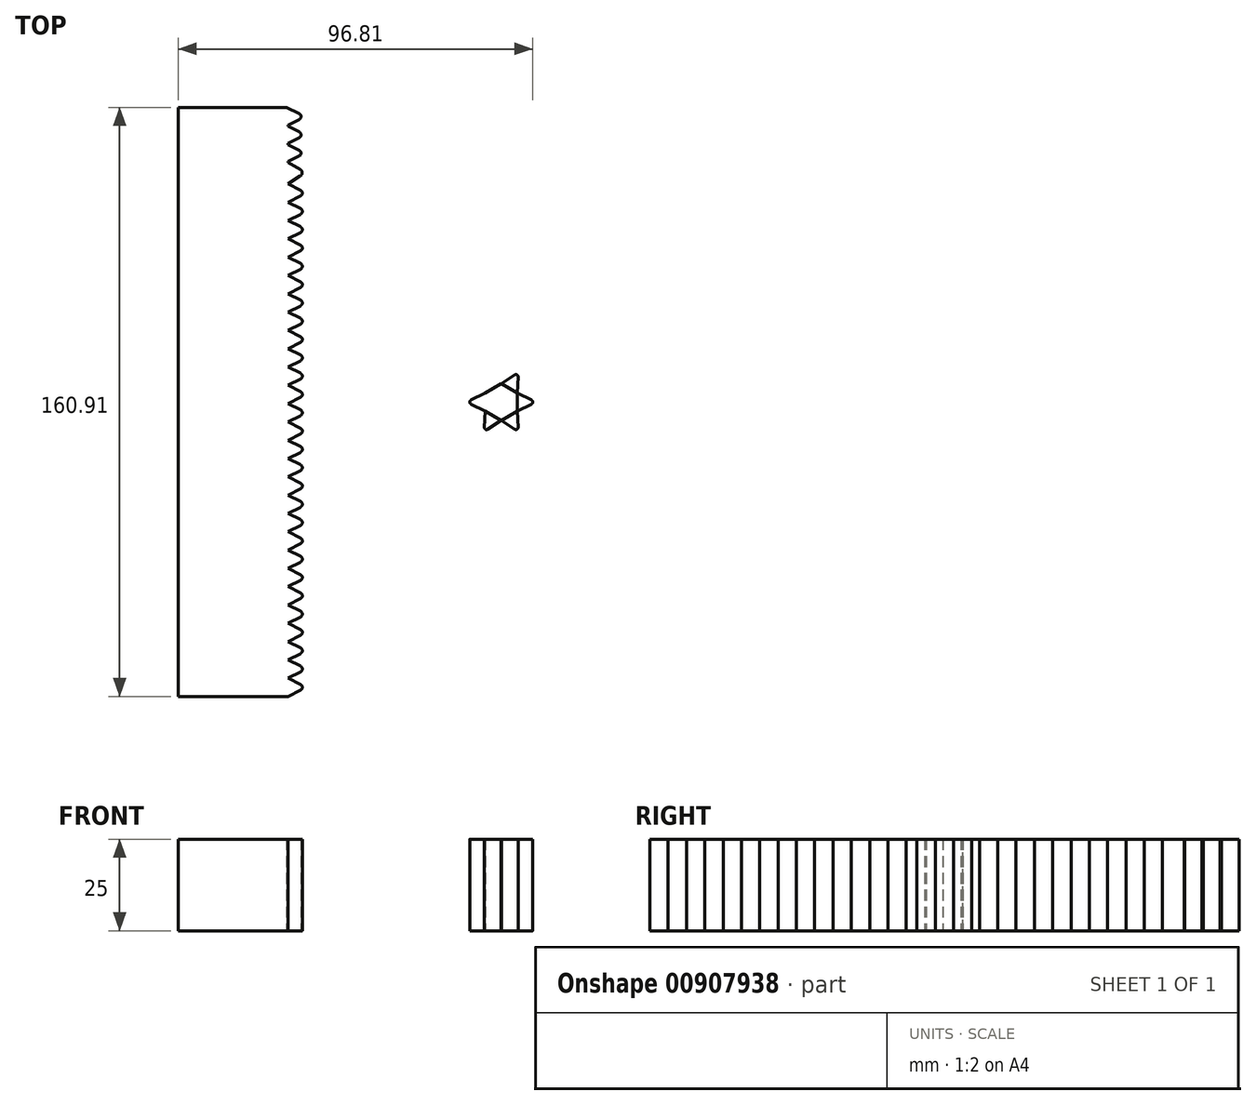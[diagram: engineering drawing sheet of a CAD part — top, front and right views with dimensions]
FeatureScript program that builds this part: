
annotation { "Feature Type Name" : "Feature", "Feature Type Description" : "" }
export const myFeature = defineFeature(function(context is Context, id is Id, definition is map)
    precondition{}
    {
        {
            var Q0;
            Q0=qCreatedBy(makeId("Top.planeOp"),FACE);
            var sketch = newSketch(context, id + "F0", { "sketchPlane" : qUnion([Q0])});
            skLineSegment(sketch, "E0.top", {"start": v(-93.92, -77.91) * mm, "end": v(-63.92, -77.91) * mm});
            skLineSegment(sketch, "E1.right", {"start": v(-63.92, -72.91) * mm, "end": v(-63.92, -77.91) * mm});
            skLineSegment(sketch, "E2", {"start": v(-63.92, -72.91) * mm, "end": v(-60.51, -74.61) * mm});
            skLineSegment(sketch, "E3", {"start": v(-60.51, -76.21) * mm, "end": v(-63.92, -77.91) * mm});
            skLineSegment(sketch, "E4.right", {"start": v(-63.92, -67.91) * mm, "end": v(-63.92, -72.91) * mm});
            skLineSegment(sketch, "E5", {"start": v(-63.92, -67.91) * mm, "end": v(-60.51, -69.61) * mm});
            skLineSegment(sketch, "E6", {"start": v(-60.51, -71.21) * mm, "end": v(-63.92, -72.91) * mm});
            skLineSegment(sketch, "E7.right", {"start": v(-63.92, -62.91) * mm, "end": v(-63.92, -67.91) * mm});
            skLineSegment(sketch, "E8", {"start": v(-63.92, -62.91) * mm, "end": v(-60.51, -64.61) * mm});
            skLineSegment(sketch, "E9", {"start": v(-60.51, -66.21) * mm, "end": v(-63.92, -67.91) * mm});
            skLineSegment(sketch, "E10.right", {"start": v(-63.92, -57.91) * mm, "end": v(-63.92, -62.91) * mm});
            skLineSegment(sketch, "E11", {"start": v(-63.92, -57.91) * mm, "end": v(-60.51, -59.61) * mm});
            skLineSegment(sketch, "E12", {"start": v(-60.51, -61.21) * mm, "end": v(-63.92, -62.91) * mm});
            skLineSegment(sketch, "E13.right", {"start": v(-63.92, -52.91) * mm, "end": v(-63.92, -57.91) * mm});
            skLineSegment(sketch, "E14", {"start": v(-63.92, -52.91) * mm, "end": v(-60.51, -54.61) * mm});
            skLineSegment(sketch, "E15", {"start": v(-60.51, -56.21) * mm, "end": v(-63.92, -57.91) * mm});
            skLineSegment(sketch, "E16.right", {"start": v(-63.92, -47.91) * mm, "end": v(-63.92, -52.91) * mm});
            skLineSegment(sketch, "E17", {"start": v(-63.92, -47.91) * mm, "end": v(-60.51, -49.61) * mm});
            skLineSegment(sketch, "E18", {"start": v(-60.51, -51.21) * mm, "end": v(-63.92, -52.91) * mm});
            skLineSegment(sketch, "E19.right", {"start": v(-63.92, -42.91) * mm, "end": v(-63.92, -47.91) * mm});
            skLineSegment(sketch, "E20", {"start": v(-63.92, -42.91) * mm, "end": v(-60.51, -44.61) * mm});
            skLineSegment(sketch, "E21", {"start": v(-60.51, -46.21) * mm, "end": v(-63.92, -47.91) * mm});
            skLineSegment(sketch, "E22.right", {"start": v(-63.92, -37.91) * mm, "end": v(-63.92, -42.91) * mm});
            skLineSegment(sketch, "E23", {"start": v(-63.92, -37.91) * mm, "end": v(-60.51, -39.61) * mm});
            skLineSegment(sketch, "E24", {"start": v(-60.51, -41.21) * mm, "end": v(-63.92, -42.91) * mm});
            skLineSegment(sketch, "E25.right", {"start": v(-63.92, -32.91) * mm, "end": v(-63.92, -37.91) * mm});
            skLineSegment(sketch, "E26", {"start": v(-63.92, -32.91) * mm, "end": v(-60.51, -34.61) * mm});
            skLineSegment(sketch, "E27", {"start": v(-60.51, -36.21) * mm, "end": v(-63.92, -37.91) * mm});
            skLineSegment(sketch, "E28.right", {"start": v(-63.92, -27.91) * mm, "end": v(-63.92, -32.91) * mm});
            skLineSegment(sketch, "E29", {"start": v(-63.92, -27.91) * mm, "end": v(-60.51, -29.61) * mm});
            skLineSegment(sketch, "E30", {"start": v(-60.51, -31.21) * mm, "end": v(-63.92, -32.91) * mm});
            skLineSegment(sketch, "E31.right", {"start": v(-63.92, -22.91) * mm, "end": v(-63.92, -27.91) * mm});
            skLineSegment(sketch, "E32", {"start": v(-63.92, -22.91) * mm, "end": v(-60.51, -24.61) * mm});
            skLineSegment(sketch, "E33", {"start": v(-60.51, -26.21) * mm, "end": v(-63.92, -27.91) * mm});
            skLineSegment(sketch, "E34.right", {"start": v(-63.92, -17.91) * mm, "end": v(-63.92, -22.91) * mm});
            skLineSegment(sketch, "E35", {"start": v(-63.92, -17.91) * mm, "end": v(-60.51, -19.61) * mm});
            skLineSegment(sketch, "E36", {"start": v(-60.51, -21.21) * mm, "end": v(-63.92, -22.91) * mm});
            skLineSegment(sketch, "E37.right", {"start": v(-63.92, -12.91) * mm, "end": v(-63.92, -17.91) * mm});
            skLineSegment(sketch, "E38", {"start": v(-63.92, -12.91) * mm, "end": v(-60.51, -14.61) * mm});
            skLineSegment(sketch, "E39", {"start": v(-60.51, -16.21) * mm, "end": v(-63.92, -17.91) * mm});
            skLineSegment(sketch, "E40.right", {"start": v(-63.92, -7.91) * mm, "end": v(-63.92, -12.91) * mm});
            skLineSegment(sketch, "E41", {"start": v(-63.92, -7.91) * mm, "end": v(-60.51, -9.61) * mm});
            skLineSegment(sketch, "E42", {"start": v(-60.51, -11.21) * mm, "end": v(-63.92, -12.91) * mm});
            skLineSegment(sketch, "E43.right", {"start": v(-63.92, -2.91) * mm, "end": v(-63.92, -7.91) * mm});
            skLineSegment(sketch, "E44", {"start": v(-63.92, -2.91) * mm, "end": v(-60.51, -4.61) * mm});
            skLineSegment(sketch, "E45", {"start": v(-60.51, -6.21) * mm, "end": v(-63.92, -7.91) * mm});
            skLineSegment(sketch, "E46.right", {"start": v(-63.92, 2.09) * mm, "end": v(-63.92, -2.91) * mm});
            skLineSegment(sketch, "E47", {"start": v(-63.92, 2.09) * mm, "end": v(-60.51, 0.39) * mm});
            skLineSegment(sketch, "E48", {"start": v(-60.51, -1.21) * mm, "end": v(-63.92, -2.91) * mm});
            skLineSegment(sketch, "E49.right", {"start": v(-63.92, 7.09) * mm, "end": v(-63.92, 2.09) * mm});
            skLineSegment(sketch, "E50", {"start": v(-63.92, 7.09) * mm, "end": v(-60.51, 5.39) * mm});
            skLineSegment(sketch, "E51", {"start": v(-60.51, 3.79) * mm, "end": v(-63.92, 2.09) * mm});
            skLineSegment(sketch, "E52.right", {"start": v(-63.92, 12.09) * mm, "end": v(-63.92, 7.09) * mm});
            skLineSegment(sketch, "E53", {"start": v(-63.92, 12.09) * mm, "end": v(-60.51, 10.39) * mm});
            skLineSegment(sketch, "E54", {"start": v(-60.51, 8.79) * mm, "end": v(-63.92, 7.09) * mm});
            skLineSegment(sketch, "E55.right", {"start": v(-63.92, 17.09) * mm, "end": v(-63.92, 12.09) * mm});
            skLineSegment(sketch, "E56", {"start": v(-63.92, 17.09) * mm, "end": v(-60.51, 15.39) * mm});
            skLineSegment(sketch, "E57", {"start": v(-60.51, 13.79) * mm, "end": v(-63.92, 12.09) * mm});
            skLineSegment(sketch, "E58.right", {"start": v(-63.92, 22.09) * mm, "end": v(-63.92, 17.09) * mm});
            skLineSegment(sketch, "E59", {"start": v(-63.92, 22.09) * mm, "end": v(-60.51, 20.39) * mm});
            skLineSegment(sketch, "E60", {"start": v(-60.51, 18.79) * mm, "end": v(-63.92, 17.09) * mm});
            skLineSegment(sketch, "E61.right", {"start": v(-63.92, 27.09) * mm, "end": v(-63.92, 22.09) * mm});
            skLineSegment(sketch, "E62", {"start": v(-63.92, 27.09) * mm, "end": v(-60.51, 25.39) * mm});
            skLineSegment(sketch, "E63", {"start": v(-60.51, 23.79) * mm, "end": v(-63.92, 22.09) * mm});
            skLineSegment(sketch, "E64.right", {"start": v(-63.92, 32.09) * mm, "end": v(-63.92, 27.09) * mm});
            skLineSegment(sketch, "E65", {"start": v(-63.92, 32.09) * mm, "end": v(-60.51, 30.39) * mm});
            skLineSegment(sketch, "E66", {"start": v(-60.51, 28.79) * mm, "end": v(-63.92, 27.09) * mm});
            skLineSegment(sketch, "E67.right", {"start": v(-63.92, 37.09) * mm, "end": v(-63.92, 32.09) * mm});
            skLineSegment(sketch, "E68", {"start": v(-63.92, 37.09) * mm, "end": v(-60.51, 35.39) * mm});
            skLineSegment(sketch, "E69", {"start": v(-60.51, 33.79) * mm, "end": v(-63.92, 32.09) * mm});
            skLineSegment(sketch, "E70.right", {"start": v(-63.92, 42.09) * mm, "end": v(-63.92, 37.09) * mm});
            skLineSegment(sketch, "E71", {"start": v(-63.92, 42.09) * mm, "end": v(-60.51, 40.39) * mm});
            skLineSegment(sketch, "E72", {"start": v(-60.51, 38.79) * mm, "end": v(-63.92, 37.09) * mm});
            skLineSegment(sketch, "E73.right", {"start": v(-63.92, 47.09) * mm, "end": v(-63.92, 42.09) * mm});
            skLineSegment(sketch, "E74", {"start": v(-63.92, 47.09) * mm, "end": v(-60.51, 45.39) * mm});
            skLineSegment(sketch, "E75", {"start": v(-60.51, 43.79) * mm, "end": v(-63.92, 42.09) * mm});
            skLineSegment(sketch, "E76.right", {"start": v(-63.92, 52.09) * mm, "end": v(-63.92, 47.09) * mm});
            skLineSegment(sketch, "E77", {"start": v(-63.92, 52.09) * mm, "end": v(-60.51, 50.39) * mm});
            skLineSegment(sketch, "E78", {"start": v(-60.51, 48.79) * mm, "end": v(-63.92, 47.09) * mm});
            skLineSegment(sketch, "E79.right", {"start": v(-63.92, 57.09) * mm, "end": v(-63.92, 52.09) * mm});
            skLineSegment(sketch, "E80", {"start": v(-63.92, 57.09) * mm, "end": v(-60.51, 55.39) * mm});
            skLineSegment(sketch, "E81", {"start": v(-60.51, 53.79) * mm, "end": v(-63.92, 52.09) * mm});
            skLineSegment(sketch, "E82.right", {"start": v(-63.92, 62.09) * mm, "end": v(-63.92, 57.09) * mm});
            skLineSegment(sketch, "E83", {"start": v(-63.92, 62.09) * mm, "end": v(-60.51, 60.39) * mm});
            skLineSegment(sketch, "E84", {"start": v(-60.51, 58.79) * mm, "end": v(-63.92, 57.09) * mm});
            skLineSegment(sketch, "E85.right", {"start": v(-63.92, 68) * mm, "end": v(-63.92, 62.09) * mm});
            skLineSegment(sketch, "E86", {"start": v(-63.92, 68) * mm, "end": v(-60.62, 66.1) * mm});
            skLineSegment(sketch, "E87", {"start": v(-60.58, 64.23) * mm, "end": v(-63.92, 62.08) * mm});
            skLineSegment(sketch, "E88.right", {"start": v(-63.92, 73) * mm, "end": v(-63.92, 68) * mm});
            skLineSegment(sketch, "E89", {"start": v(-64.28, 73) * mm, "end": v(-60.88, 71.3) * mm});
            skLineSegment(sketch, "E90", {"start": v(-60.88, 69.7) * mm, "end": v(-63.92, 68.18) * mm});
            skLineSegment(sketch, "E91.right", {"start": v(-63.92, 78) * mm, "end": v(-63.92, 73) * mm});
            skLineSegment(sketch, "E92", {"start": v(-64.28, 78) * mm, "end": v(-60.88, 76.3) * mm});
            skLineSegment(sketch, "E93", {"start": v(-60.88, 74.7) * mm, "end": v(-63.92, 73.18) * mm});
            skLineSegment(sketch, "E94.right", {"start": v(-63.92, 83) * mm, "end": v(-63.92, 78) * mm});
            skLineSegment(sketch, "E95", {"start": v(-64.28, 83) * mm, "end": v(-60.88, 81.3) * mm});
            skLineSegment(sketch, "E96", {"start": v(-60.88, 79.7) * mm, "end": v(-63.92, 78.18) * mm});
            skPoint(sketch, "E97.visualSharp", {"position": v(-59.28, 80.5) * mm});
            skArc(sketch, "E97.filletArc", {"start": v(-60.88, 79.7) * mm, "mid": v(-60.38, 80.5) * mm, "end": v(-60.88, 81.3) * mm});
            skPoint(sketch, "E98.visualSharp", {"position": v(-59.28, 75.5) * mm});
            skArc(sketch, "E98.filletArc", {"start": v(-60.88, 74.7) * mm, "mid": v(-60.38, 75.5) * mm, "end": v(-60.88, 76.3) * mm});
            skPoint(sketch, "E99.visualSharp", {"position": v(-59.28, 70.5) * mm});
            skArc(sketch, "E99.filletArc", {"start": v(-60.88, 69.7) * mm, "mid": v(-60.38, 70.5) * mm, "end": v(-60.88, 71.3) * mm});
            skPoint(sketch, "E100.visualSharp", {"position": v(-59.08, 65.2) * mm});
            skArc(sketch, "E100.filletArc", {"start": v(-60.58, 64.23) * mm, "mid": v(-60.08, 65.18) * mm, "end": v(-60.62, 66.1) * mm});
            skPoint(sketch, "E101.visualSharp", {"position": v(-58.92, 59.59) * mm});
            skArc(sketch, "E101.filletArc", {"start": v(-60.51, 58.79) * mm, "mid": v(-60.02, 59.59) * mm, "end": v(-60.51, 60.39) * mm});
            skPoint(sketch, "E102.visualSharp", {"position": v(-58.92, 54.59) * mm});
            skArc(sketch, "E102.filletArc", {"start": v(-60.51, 53.79) * mm, "mid": v(-60.02, 54.59) * mm, "end": v(-60.51, 55.39) * mm});
            skPoint(sketch, "E103.visualSharp", {"position": v(-58.92, 49.59) * mm});
            skArc(sketch, "E103.filletArc", {"start": v(-60.51, 48.79) * mm, "mid": v(-60.02, 49.59) * mm, "end": v(-60.51, 50.39) * mm});
            skPoint(sketch, "E104.visualSharp", {"position": v(-58.92, 44.59) * mm});
            skArc(sketch, "E104.filletArc", {"start": v(-60.51, 43.79) * mm, "mid": v(-60.02, 44.59) * mm, "end": v(-60.51, 45.39) * mm});
            skPoint(sketch, "E105.visualSharp", {"position": v(-58.92, 39.59) * mm});
            skArc(sketch, "E105.filletArc", {"start": v(-60.51, 38.79) * mm, "mid": v(-60.02, 39.59) * mm, "end": v(-60.51, 40.39) * mm});
            skPoint(sketch, "E106.visualSharp", {"position": v(-58.92, 34.59) * mm});
            skArc(sketch, "E106.filletArc", {"start": v(-60.51, 33.79) * mm, "mid": v(-60.02, 34.59) * mm, "end": v(-60.51, 35.39) * mm});
            skPoint(sketch, "E107.visualSharp", {"position": v(-58.92, 29.59) * mm});
            skArc(sketch, "E107.filletArc", {"start": v(-60.51, 28.79) * mm, "mid": v(-60.02, 29.59) * mm, "end": v(-60.51, 30.39) * mm});
            skPoint(sketch, "E108.visualSharp", {"position": v(-58.92, 24.59) * mm});
            skArc(sketch, "E108.filletArc", {"start": v(-60.51, 23.79) * mm, "mid": v(-60.02, 24.59) * mm, "end": v(-60.51, 25.39) * mm});
            skPoint(sketch, "E109.visualSharp", {"position": v(-58.92, 19.59) * mm});
            skArc(sketch, "E109.filletArc", {"start": v(-60.51, 18.79) * mm, "mid": v(-60.02, 19.59) * mm, "end": v(-60.51, 20.39) * mm});
            skPoint(sketch, "E110.visualSharp", {"position": v(-58.92, 14.59) * mm});
            skArc(sketch, "E110.filletArc", {"start": v(-60.51, 13.79) * mm, "mid": v(-60.02, 14.59) * mm, "end": v(-60.51, 15.39) * mm});
            skPoint(sketch, "E111.visualSharp", {"position": v(-58.92, 9.59) * mm});
            skArc(sketch, "E111.filletArc", {"start": v(-60.51, 8.79) * mm, "mid": v(-60.02, 9.59) * mm, "end": v(-60.51, 10.39) * mm});
            skPoint(sketch, "E112.visualSharp", {"position": v(-58.92, 4.59) * mm});
            skArc(sketch, "E112.filletArc", {"start": v(-60.51, 3.79) * mm, "mid": v(-60.02, 4.59) * mm, "end": v(-60.51, 5.39) * mm});
            skPoint(sketch, "E113.visualSharp", {"position": v(-58.92, -0.41) * mm});
            skArc(sketch, "E113.filletArc", {"start": v(-60.51, -1.21) * mm, "mid": v(-60.02, -0.41) * mm, "end": v(-60.51, 0.39) * mm});
            skPoint(sketch, "E114.visualSharp", {"position": v(-58.92, -5.41) * mm});
            skArc(sketch, "E114.filletArc", {"start": v(-60.51, -6.21) * mm, "mid": v(-60.02, -5.41) * mm, "end": v(-60.51, -4.61) * mm});
            skPoint(sketch, "E115.visualSharp", {"position": v(-58.92, -10.41) * mm});
            skArc(sketch, "E115.filletArc", {"start": v(-60.51, -11.21) * mm, "mid": v(-60.02, -10.41) * mm, "end": v(-60.51, -9.61) * mm});
            skPoint(sketch, "E116.visualSharp", {"position": v(-58.92, -15.41) * mm});
            skArc(sketch, "E116.filletArc", {"start": v(-60.51, -16.21) * mm, "mid": v(-60.02, -15.41) * mm, "end": v(-60.51, -14.61) * mm});
            skPoint(sketch, "E117.visualSharp", {"position": v(-58.92, -20.41) * mm});
            skArc(sketch, "E117.filletArc", {"start": v(-60.51, -21.21) * mm, "mid": v(-60.02, -20.41) * mm, "end": v(-60.51, -19.61) * mm});
            skPoint(sketch, "E118.visualSharp", {"position": v(-58.92, -25.41) * mm});
            skArc(sketch, "E118.filletArc", {"start": v(-60.51, -26.21) * mm, "mid": v(-60.02, -25.41) * mm, "end": v(-60.51, -24.61) * mm});
            skPoint(sketch, "E119.visualSharp", {"position": v(-58.92, -30.41) * mm});
            skArc(sketch, "E119.filletArc", {"start": v(-60.51, -31.21) * mm, "mid": v(-60.02, -30.41) * mm, "end": v(-60.51, -29.61) * mm});
            skPoint(sketch, "E120.visualSharp", {"position": v(-58.92, -35.41) * mm});
            skArc(sketch, "E120.filletArc", {"start": v(-60.51, -36.21) * mm, "mid": v(-60.02, -35.41) * mm, "end": v(-60.51, -34.61) * mm});
            skPoint(sketch, "E121.visualSharp", {"position": v(-58.92, -40.41) * mm});
            skArc(sketch, "E121.filletArc", {"start": v(-60.51, -41.21) * mm, "mid": v(-60.02, -40.41) * mm, "end": v(-60.51, -39.61) * mm});
            skPoint(sketch, "E122.visualSharp", {"position": v(-58.92, -45.41) * mm});
            skArc(sketch, "E122.filletArc", {"start": v(-60.51, -46.21) * mm, "mid": v(-60.02, -45.41) * mm, "end": v(-60.51, -44.61) * mm});
            skPoint(sketch, "E123.visualSharp", {"position": v(-58.92, -50.41) * mm});
            skArc(sketch, "E123.filletArc", {"start": v(-60.51, -51.21) * mm, "mid": v(-60.02, -50.41) * mm, "end": v(-60.51, -49.61) * mm});
            skPoint(sketch, "E124.visualSharp", {"position": v(-58.92, -55.41) * mm});
            skArc(sketch, "E124.filletArc", {"start": v(-60.51, -56.21) * mm, "mid": v(-60.02, -55.41) * mm, "end": v(-60.51, -54.61) * mm});
            skPoint(sketch, "E125.visualSharp", {"position": v(-58.92, -60.41) * mm});
            skArc(sketch, "E125.filletArc", {"start": v(-60.51, -61.21) * mm, "mid": v(-60.02, -60.41) * mm, "end": v(-60.51, -59.61) * mm});
            skPoint(sketch, "E126.visualSharp", {"position": v(-58.92, -65.41) * mm});
            skArc(sketch, "E126.filletArc", {"start": v(-60.51, -66.21) * mm, "mid": v(-60.02, -65.41) * mm, "end": v(-60.51, -64.61) * mm});
            skPoint(sketch, "E127.visualSharp", {"position": v(-58.92, -70.41) * mm});
            skArc(sketch, "E127.filletArc", {"start": v(-60.51, -71.21) * mm, "mid": v(-60.02, -70.41) * mm, "end": v(-60.51, -69.61) * mm});
            skPoint(sketch, "E128.visualSharp", {"position": v(-58.92, -75.41) * mm});
            skArc(sketch, "E128.filletArc", {"start": v(-60.51, -76.21) * mm, "mid": v(-60.02, -75.41) * mm, "end": v(-60.51, -74.61) * mm});
            skLineSegment(sketch, "E129", {"start": v(-63.92, 83) * mm, "end": v(-93.92, 83) * mm});
            skLineSegment(sketch, "E130", {"start": v(-93.92, 83) * mm, "end": v(-93.92, -77.91) * mm});
            skSolve(sketch);
        }
        {
            var Q0;
            Q0=makeQuery(id+"F0.imprint","IMPRINT",FACE,{"disambiguationData":[TD([[makeQuery(id+"F0.imprint","IMPRINT",EDGE,{"derivedFrom":sQuery(id+"F0.wireOp",EDGE,"E0.top")}),1.0]])]});
            var Q1;
            Q1=makeQuery(id+"F0.imprint","IMPRINT",FACE,{"disambiguationData":[TD([[makeQuery(id+"F0.imprint","IMPRINT",EDGE,{"derivedFrom":sQuery(id+"F0.wireOp",EDGE,"E52.right")}),1.0]])]});
            var Q2;
            Q2=makeQuery(id+"F0.imprint","IMPRINT",FACE,{"disambiguationData":[TD([[makeQuery(id+"F0.imprint","IMPRINT",EDGE,{"derivedFrom":sQuery(id+"F0.wireOp",EDGE,"E22.right")}),1.0]])]});
            var Q3;
            Q3=makeQuery(id+"F0.imprint","IMPRINT",FACE,{"disambiguationData":[TD([[makeQuery(id+"F0.imprint","IMPRINT",EDGE,{"derivedFrom":sQuery(id+"F0.wireOp",EDGE,"E70.right")}),1.0]])]});
            var Q4;
            Q4=makeQuery(id+"F0.imprint","IMPRINT",FACE,{"disambiguationData":[TD([[makeQuery(id+"F0.imprint","IMPRINT",EDGE,{"derivedFrom":sQuery(id+"F0.wireOp",EDGE,"E13.right")}),1.0]])]});
            var Q5;
            Q5=makeQuery(id+"F0.imprint","IMPRINT",FACE,{"disambiguationData":[TD([[makeQuery(id+"F0.imprint","IMPRINT",EDGE,{"derivedFrom":sQuery(id+"F0.wireOp",EDGE,"E91.right")}),1.0]])]});
            var Q6;
            Q6=makeQuery(id+"F0.imprint","IMPRINT",FACE,{"disambiguationData":[TD([[makeQuery(id+"F0.imprint","IMPRINT",EDGE,{"derivedFrom":sQuery(id+"F0.wireOp",EDGE,"E61.right")}),1.0]])]});
            var Q7;
            Q7=makeQuery(id+"F0.imprint","IMPRINT",FACE,{"disambiguationData":[TD([[makeQuery(id+"F0.imprint","IMPRINT",EDGE,{"derivedFrom":sQuery(id+"F0.wireOp",EDGE,"E31.right")}),1.0]])]});
            var Q8;
            Q8=makeQuery(id+"F0.imprint","IMPRINT",FACE,{"disambiguationData":[TD([[makeQuery(id+"F0.imprint","IMPRINT",EDGE,{"derivedFrom":sQuery(id+"F0.wireOp",EDGE,"E4.right")}),1.0]])]});
            var Q9;
            Q9=makeQuery(id+"F0.imprint","IMPRINT",FACE,{"disambiguationData":[TD([[makeQuery(id+"F0.imprint","IMPRINT",EDGE,{"derivedFrom":sQuery(id+"F0.wireOp",EDGE,"E43.right")}),1.0]])]});
            var Q10;
            Q10=makeQuery(id+"F0.imprint","IMPRINT",FACE,{"disambiguationData":[TD([[makeQuery(id+"F0.imprint","IMPRINT",EDGE,{"derivedFrom":sQuery(id+"F0.wireOp",EDGE,"E79.right")}),1.0]])]});
            var Q11;
            Q11=makeQuery(id+"F0.imprint","IMPRINT",FACE,{"disambiguationData":[TD([[makeQuery(id+"F0.imprint","IMPRINT",EDGE,{"derivedFrom":sQuery(id+"F0.wireOp",EDGE,"E85.right")}),1.0]])]});
            var Q12;
            Q12=makeQuery(id+"F0.imprint","IMPRINT",FACE,{"disambiguationData":[TD([[makeQuery(id+"F0.imprint","IMPRINT",EDGE,{"derivedFrom":sQuery(id+"F0.wireOp",EDGE,"E55.right")}),1.0]])]});
            var Q13;
            Q13=makeQuery(id+"F0.imprint","IMPRINT",FACE,{"disambiguationData":[TD([[makeQuery(id+"F0.imprint","IMPRINT",EDGE,{"derivedFrom":sQuery(id+"F0.wireOp",EDGE,"E40.right")}),1.0]])]});
            var Q14;
            Q14=makeQuery(id+"F0.imprint","IMPRINT",FACE,{"disambiguationData":[TD([[makeQuery(id+"F0.imprint","IMPRINT",EDGE,{"derivedFrom":sQuery(id+"F0.wireOp",EDGE,"E7.right")}),1.0]])]});
            var Q15;
            {var subQ1=sQuery(id+"F0.wireOp",EDGE,"E95");Q15=makeQuery(id+"F0.imprint","IMPRINT",FACE,{"disambiguationData":[TD([[makeQuery(id+"F0.imprint","IMPRINT",EDGE,{"derivedFrom":subQ1}),-1.0]])]});}
            var Q16;
            Q16=makeQuery(id+"F0.imprint","IMPRINT",FACE,{"disambiguationData":[TD([[makeQuery(id+"F0.imprint","IMPRINT",EDGE,{"derivedFrom":sQuery(id+"F0.wireOp",EDGE,"E67.right")}),1.0]])]});
            var Q17;
            Q17=makeQuery(id+"F0.imprint","IMPRINT",FACE,{"disambiguationData":[TD([[makeQuery(id+"F0.imprint","IMPRINT",EDGE,{"derivedFrom":sQuery(id+"F0.wireOp",EDGE,"E73.right")}),1.0]])]});
            var Q18;
            Q18=makeQuery(id+"F0.imprint","IMPRINT",FACE,{"disambiguationData":[TD([[makeQuery(id+"F0.imprint","IMPRINT",EDGE,{"derivedFrom":sQuery(id+"F0.wireOp",EDGE,"E19.right")}),1.0]])]});
            var Q19;
            Q19=makeQuery(id+"F0.imprint","IMPRINT",FACE,{"disambiguationData":[TD([[makeQuery(id+"F0.imprint","IMPRINT",EDGE,{"derivedFrom":sQuery(id+"F0.wireOp",EDGE,"E88.right")}),1.0]])]});
            var Q20;
            Q20=makeQuery(id+"F0.imprint","IMPRINT",FACE,{"disambiguationData":[TD([[makeQuery(id+"F0.imprint","IMPRINT",EDGE,{"derivedFrom":sQuery(id+"F0.wireOp",EDGE,"E25.right")}),1.0]])]});
            var Q21;
            Q21=makeQuery(id+"F0.imprint","IMPRINT",FACE,{"disambiguationData":[TD([[makeQuery(id+"F0.imprint","IMPRINT",EDGE,{"derivedFrom":sQuery(id+"F0.wireOp",EDGE,"E82.right")}),1.0]])]});
            var Q22;
            Q22=makeQuery(id+"F0.imprint","IMPRINT",FACE,{"disambiguationData":[TD([[makeQuery(id+"F0.imprint","IMPRINT",EDGE,{"derivedFrom":sQuery(id+"F0.wireOp",EDGE,"E1.right")}),1.0]])]});
            var Q23;
            Q23=makeQuery(id+"F0.imprint","IMPRINT",FACE,{"disambiguationData":[TD([[makeQuery(id+"F0.imprint","IMPRINT",EDGE,{"derivedFrom":sQuery(id+"F0.wireOp",EDGE,"E28.right")}),1.0]])]});
            var Q24;
            Q24=makeQuery(id+"F0.imprint","IMPRINT",FACE,{"disambiguationData":[TD([[makeQuery(id+"F0.imprint","IMPRINT",EDGE,{"derivedFrom":sQuery(id+"F0.wireOp",EDGE,"E76.right")}),1.0]])]});
            var Q25;
            Q25=makeQuery(id+"F0.imprint","IMPRINT",FACE,{"disambiguationData":[TD([[makeQuery(id+"F0.imprint","IMPRINT",EDGE,{"derivedFrom":sQuery(id+"F0.wireOp",EDGE,"E49.right")}),1.0]])]});
            var Q26;
            Q26=makeQuery(id+"F0.imprint","IMPRINT",FACE,{"disambiguationData":[TD([[makeQuery(id+"F0.imprint","IMPRINT",EDGE,{"derivedFrom":sQuery(id+"F0.wireOp",EDGE,"E58.right")}),1.0]])]});
            var Q27;
            Q27=makeQuery(id+"F0.imprint","IMPRINT",FACE,{"disambiguationData":[TD([[makeQuery(id+"F0.imprint","IMPRINT",EDGE,{"derivedFrom":sQuery(id+"F0.wireOp",EDGE,"E37.right")}),1.0]])]});
            var Q28;
            Q28=makeQuery(id+"F0.imprint","IMPRINT",FACE,{"disambiguationData":[TD([[makeQuery(id+"F0.imprint","IMPRINT",EDGE,{"derivedFrom":sQuery(id+"F0.wireOp",EDGE,"E64.right")}),1.0]])]});
            var Q29;
            Q29=makeQuery(id+"F0.imprint","IMPRINT",FACE,{"disambiguationData":[TD([[makeQuery(id+"F0.imprint","IMPRINT",EDGE,{"derivedFrom":sQuery(id+"F0.wireOp",EDGE,"E46.right")}),1.0]])]});
            var Q30;
            Q30=makeQuery(id+"F0.imprint","IMPRINT",FACE,{"disambiguationData":[TD([[makeQuery(id+"F0.imprint","IMPRINT",EDGE,{"derivedFrom":sQuery(id+"F0.wireOp",EDGE,"E10.right")}),1.0]])]});
            var Q31;
            Q31=makeQuery(id+"F0.imprint","IMPRINT",FACE,{"disambiguationData":[TD([[makeQuery(id+"F0.imprint","IMPRINT",EDGE,{"derivedFrom":sQuery(id+"F0.wireOp",EDGE,"E16.right")}),1.0]])]});
            var Q32;
            Q32=makeQuery(id+"F0.imprint","IMPRINT",FACE,{"disambiguationData":[TD([[makeQuery(id+"F0.imprint","IMPRINT",EDGE,{"derivedFrom":sQuery(id+"F0.wireOp",EDGE,"E34.right")}),1.0]])]});
            var Q33;
            {var subQ0=sQuery(id+"F0.wireOp",EDGE,"E84");Q33=makeQuery(id+"F0.imprint","IMPRINT",FACE,{"disambiguationData":[TD([[makeQuery(id+"F0.imprint","IMPRINT",EDGE,{"derivedFrom":subQ0}),-1.0]])]});}
            extrude(context, id + "F1", {"entities" : qUnion([Q0, Q1, Q2, Q3, Q4, Q5, Q6, Q7, Q8, Q9, Q10, Q11, Q12, Q13, Q14, Q15, Q16, Q17, Q18, Q19, Q20, Q21, Q22, Q23, Q24, Q25, Q26, Q27, Q28, Q29, Q30, Q31, Q32, Q33]), "depth" : 25 * mm, "offsetDistance" : 25 * mm});
        }
        {
            var Q0;
            Q0=qCreatedBy(makeId("Top.planeOp"),FACE);
            var sketch = newSketch(context, id + "F2", { "sketchPlane" : qUnion([Q0])});
            skLineSegment(sketch, "E131", {"start": v(-10.04, 5) * mm, "end": v(-10.04, 0) * mm});
            skLineSegment(sketch, "E132", {"start": v(-10.04, 5) * mm, "end": v(-13.97, 3.03) * mm});
            skLineSegment(sketch, "E133", {"start": v(-13.97, 1.97) * mm, "end": v(-10.04, 0) * mm});
            skPoint(sketch, "E134", {"position": v(-10.04, 2.5) * mm});
            skPoint(sketch, "E135.visualSharp", {"position": v(-15.04, 2.5) * mm});
            skArc(sketch, "E135.filletArc", {"start": v(-13.97, 3.03) * mm, "mid": v(-14.3, 2.5) * mm, "end": v(-13.97, 1.97) * mm});
            skLineSegment(sketch, "E136.0", {"start": v(-10.04, 0) * mm, "end": v(-10.04, 5) * mm});
            skLineSegment(sketch, "E136.1", {"start": v(-10.04, 5) * mm, "end": v(-5.7, 7.5) * mm});
            skLineSegment(sketch, "E136.2", {"start": v(-5.7, 7.5) * mm, "end": v(-1.38, 5) * mm});
            skLineSegment(sketch, "E136.3", {"start": v(-1.38, 5) * mm, "end": v(-1.38, 0) * mm});
            skLineSegment(sketch, "E136.4", {"start": v(-1.38, 0) * mm, "end": v(-5.7, -2.5) * mm});
            skLineSegment(sketch, "E136.5", {"start": v(-5.7, -2.5) * mm, "end": v(-10.04, 0) * mm});
            skLineSegment(sketch, "E137", {"start": v(-1.38, 0) * mm, "end": v(2.56, 1.97) * mm});
            skLineSegment(sketch, "E138", {"start": v(2.56, 3.03) * mm, "end": v(-1.38, 5) * mm});
            skArc(sketch, "E139.filletArc", {"start": v(2.56, 1.97) * mm, "mid": v(2.89, 2.5) * mm, "end": v(2.56, 3.03) * mm});
            skLineSegment(sketch, "E140", {"start": v(-10.04, 0) * mm, "end": v(-5.7, -2.5) * mm});
            skLineSegment(sketch, "E141", {"start": v(-10.04, 0) * mm, "end": v(-10.3, -4.4) * mm});
            skLineSegment(sketch, "E142", {"start": v(-9.38, -4.92) * mm, "end": v(-5.7, -2.5) * mm});
            skPoint(sketch, "E143", {"position": v(-7.87, -1.25) * mm});
            skPoint(sketch, "E144.visualSharp", {"position": v(-10.37, -5.58) * mm});
            skArc(sketch, "E144.filletArc", {"start": v(-10.3, -4.4) * mm, "mid": v(-10, -4.94) * mm, "end": v(-9.38, -4.92) * mm});
            skLineSegment(sketch, "E145.3", {"start": v(-5.7, 7.5) * mm, "end": v(-1.37, 5) * mm});
            skLineSegment(sketch, "E145.4", {"start": v(-1.37, 5) * mm, "end": v(-1.37, 0) * mm});
            skLineSegment(sketch, "E145.5", {"start": v(-1.37, 0) * mm, "end": v(-5.7, -2.5) * mm});
            skLineSegment(sketch, "E146", {"start": v(-1.38, 5) * mm, "end": v(-1.11, 9.4) * mm});
            skLineSegment(sketch, "E147", {"start": v(-2.03, 9.92) * mm, "end": v(-5.7, 7.5) * mm});
            skArc(sketch, "E148.filletArc", {"start": v(-1.11, 9.4) * mm, "mid": v(-1.4, 9.94) * mm, "end": v(-2.03, 9.92) * mm});
            skLineSegment(sketch, "E149.0", {"start": v(-10.37, -5.58) * mm, "end": v(-7.87, -1.25) * mm, "construction": true});
            skLineSegment(sketch, "E150", {"start": v(-5.7, -2.5) * mm, "end": v(-1.37, 0) * mm});
            skLineSegment(sketch, "E151", {"start": v(-5.7, -2.5) * mm, "end": v(-2.03, -4.92) * mm});
            skLineSegment(sketch, "E152", {"start": v(-1.1, -4.39) * mm, "end": v(-1.37, 0) * mm});
            skPoint(sketch, "E153", {"position": v(-3.53, -1.24) * mm});
            skPoint(sketch, "E154.visualSharp", {"position": v(-1.03, -5.57) * mm});
            skArc(sketch, "E154.filletArc", {"start": v(-2.03, -4.92) * mm, "mid": v(-1.4, -4.94) * mm, "end": v(-1.1, -4.39) * mm});
            skLineSegment(sketch, "E155.1", {"start": v(-5.7, -2.5) * mm, "end": v(-10.03, 0) * mm});
            skLineSegment(sketch, "E155.2", {"start": v(-10.03, 0) * mm, "end": v(-10.03, 5) * mm});
            skLineSegment(sketch, "E155.3", {"start": v(-10.03, 5) * mm, "end": v(-5.7, 7.5) * mm});
            skLineSegment(sketch, "E156", {"start": v(-5.7, 7.5) * mm, "end": v(-9.37, 9.93) * mm});
            skLineSegment(sketch, "E157", {"start": v(-10.3, 9.4) * mm, "end": v(-10.03, 5) * mm});
            skArc(sketch, "E158.filletArc", {"start": v(-9.37, 9.93) * mm, "mid": v(-10, 9.95) * mm, "end": v(-10.3, 9.4) * mm});
            skLineSegment(sketch, "E159.0", {"start": v(-1.03, -5.57) * mm, "end": v(-3.53, -1.24) * mm, "construction": true});
            skSolve(sketch);
        }
        {
            var Q0;
            {var subQ0=sQuery(id+"F2.wireOp",EDGE,"E145.3");Q0=makeQuery(id+"F2.imprint","IMPRINT",FACE,{"disambiguationData":[TD([[makeQuery(id+"F2.imprint","IMPRINT",EDGE,{"derivedFrom":subQ0}),1.0]])]});}
            var Q1;
            {var subQ0=sQuery(id+"F2.wireOp",EDGE,"E148.filletArc");Q1=makeQuery(id+"F2.imprint","IMPRINT",FACE,{"disambiguationData":[TD([[makeQuery(id+"F2.imprint","IMPRINT",EDGE,{"derivedFrom":subQ0}),1.0]])]});}
            var Q2;
            {var subQ0=sQuery(id+"F2.wireOp",EDGE,"E139.filletArc");Q2=makeQuery(id+"F2.imprint","IMPRINT",FACE,{"disambiguationData":[TD([[makeQuery(id+"F2.imprint","IMPRINT",EDGE,{"derivedFrom":subQ0}),1.0]])]});}
            var Q3;
            {var subQ5=sQuery(id+"F2.wireOp",EDGE,"E154.filletArc");Q3=makeQuery(id+"F2.imprint","IMPRINT",FACE,{"disambiguationData":[TD([[makeQuery(id+"F2.imprint","IMPRINT",EDGE,{"derivedFrom":subQ5}),1.0]])]});}
            var Q4;
            {var subQ6=sQuery(id+"F2.wireOp",EDGE,"E141");Q4=makeQuery(id+"F2.imprint","IMPRINT",FACE,{"disambiguationData":[TD([[makeQuery(id+"F2.imprint","IMPRINT",EDGE,{"derivedFrom":subQ6}),1.0]])]});}
            var Q5;
            {var subQ0=sQuery(id+"F2.wireOp",EDGE,"E132");Q5=makeQuery(id+"F2.imprint","IMPRINT",FACE,{"disambiguationData":[TD([[makeQuery(id+"F2.imprint","IMPRINT",EDGE,{"derivedFrom":subQ0}),1.0]])]});}
            var Q6;
            {var subQ5=sQuery(id+"F2.wireOp",EDGE,"E136.1");Q6=makeQuery(id+"F2.imprint","IMPRINT",FACE,{"disambiguationData":[TD([[makeQuery(id+"F2.imprint","IMPRINT",EDGE,{"derivedFrom":subQ5}),-1.0]])]});}
            extrude(context, id + "F3", {"entities" : qUnion([Q0, Q1, Q2, Q3, Q4, Q5, Q6]), "depth" : 25 * mm, "offsetDistance" : 25 * mm});
        }
        {
            var Q0;
            Q0=makeQuery(id+"F3.opExtrude","SWEPT_BODY",BODY,{"disambiguationData":[OSD([sQuery(id+"F2.wireOp",EDGE,"E137"),sQuery(id+"F2.wireOp",EDGE,"E145.4"),sQuery(id+"F2.wireOp",EDGE,"E145.5"),sQuery(id+"F2.wireOp",EDGE,"E151"),sQuery(id+"F2.wireOp",EDGE,"E152"),sQuery(id+"F2.wireOp",EDGE,"E154.filletArc")])]});
            var Q1;
            Q1=makeQuery(id+"F3.opExtrude","SWEPT_BODY",BODY,{"disambiguationData":[OSD([sQuery(id+"F2.wireOp",EDGE,"E136.1"),sQuery(id+"F2.wireOp",EDGE,"E136.2"),sQuery(id+"F2.wireOp",EDGE,"E136.3"),sQuery(id+"F2.wireOp",EDGE,"E145.5"),sQuery(id+"F2.wireOp",EDGE,"E155.1"),sQuery(id+"F2.wireOp",EDGE,"E155.2")])]});
            var Q2;
            Q2=makeQuery(id+"F3.opExtrude","SWEPT_BODY",BODY,{"disambiguationData":[OSD([sQuery(id+"F2.wireOp",EDGE,"E132"),sQuery(id+"F2.wireOp",EDGE,"E133"),sQuery(id+"F2.wireOp",EDGE,"E135.filletArc"),sQuery(id+"F2.wireOp",EDGE,"E136.0")])]});
            var Q3;
            Q3=makeQuery(id+"F3.opExtrude","SWEPT_BODY",BODY,{"disambiguationData":[OSD([sQuery(id+"F2.wireOp",EDGE,"E137"),sQuery(id+"F2.wireOp",EDGE,"E138"),sQuery(id+"F2.wireOp",EDGE,"E139.filletArc"),sQuery(id+"F2.wireOp",EDGE,"E152"),sQuery(id+"F2.wireOp",EDGE,"E145.4")])]});
            var Q4;
            Q4=makeQuery(id+"F3.opExtrude","SWEPT_BODY",BODY,{"disambiguationData":[OSD([sQuery(id+"F2.wireOp",EDGE,"E141"),sQuery(id+"F2.wireOp",EDGE,"E142"),sQuery(id+"F2.wireOp",EDGE,"E144.filletArc"),sQuery(id+"F2.wireOp",EDGE,"E136.5"),sQuery(id+"F2.wireOp",EDGE,"E136.0")])]});
            var Q5;
            Q5=makeQuery(id+"F3.opExtrude","SWEPT_BODY",BODY,{"disambiguationData":[OSD([sQuery(id+"F2.wireOp",EDGE,"E136.1"),sQuery(id+"F2.wireOp",EDGE,"E145.3"),sQuery(id+"F2.wireOp",EDGE,"E155.3"),sQuery(id+"F2.wireOp",EDGE,"E156"),sQuery(id+"F2.wireOp",EDGE,"E157"),sQuery(id+"F2.wireOp",EDGE,"E158.filletArc")])]});
            var Q6;
            Q6=makeQuery(id+"F3.opExtrude","SWEPT_BODY",BODY,{"disambiguationData":[OSD([sQuery(id+"F2.wireOp",EDGE,"E146"),sQuery(id+"F2.wireOp",EDGE,"E147"),sQuery(id+"F2.wireOp",EDGE,"E148.filletArc"),sQuery(id+"F2.wireOp",EDGE,"E145.3")])]});
            booleanBodies(context, id + "F4", {"operationType" : BooleanOperationType.UNION, "tools" : qUnion([Q0, Q1, Q2, Q3, Q4, Q5, Q6])});
        }
        {
            var Q0;
            Q0=makeQuery(id+"F3.opExtrude","SWEPT_BODY",BODY,{"disambiguationData":[OSD([sQuery(id+"F2.wireOp",EDGE,"E146"),sQuery(id+"F2.wireOp",EDGE,"E147"),sQuery(id+"F2.wireOp",EDGE,"E148.filletArc"),sQuery(id+"F2.wireOp",EDGE,"E145.3")])]});
            var Q1;
            {var subQ0=sQuery(id+"F2.wireOp",EDGE,"E136.0");Q1=makeQuery(id+"F4.opBoolean","MERGE",BODY,{"derivedFrom":[makeQuery(id+"F3.opExtrude","SWEPT_BODY",BODY,{"disambiguationData":[OSD([sQuery(id+"F2.wireOp",EDGE,"E132"),sQuery(id+"F2.wireOp",EDGE,"E133"),sQuery(id+"F2.wireOp",EDGE,"E135.filletArc"),subQ0])]}),makeQuery(id+"F3.opExtrude","SWEPT_BODY",BODY,{"disambiguationData":[OSD([sQuery(id+"F2.wireOp",EDGE,"E136.1"),sQuery(id+"F2.wireOp",EDGE,"E136.2"),sQuery(id+"F2.wireOp",EDGE,"E136.3"),sQuery(id+"F2.wireOp",EDGE,"E145.5"),sQuery(id+"F2.wireOp",EDGE,"E155.1"),sQuery(id+"F2.wireOp",EDGE,"E155.2")])]}),makeQuery(id+"F3.opExtrude","SWEPT_BODY",BODY,{"disambiguationData":[OSD([sQuery(id+"F2.wireOp",EDGE,"E141"),sQuery(id+"F2.wireOp",EDGE,"E142"),sQuery(id+"F2.wireOp",EDGE,"E144.filletArc"),sQuery(id+"F2.wireOp",EDGE,"E136.5"),subQ0])]})]});}
            var Q2;
            {var subQ0=sQuery(id+"F2.wireOp",EDGE,"E152");var subQ1=sQuery(id+"F2.wireOp",EDGE,"E137");Q2=makeQuery(id+"F4.opBoolean","MERGE",BODY,{"derivedFrom":[makeQuery(id+"F3.opExtrude","SWEPT_BODY",BODY,{"disambiguationData":[OSD([subQ1,sQuery(id+"F2.wireOp",EDGE,"E145.4"),sQuery(id+"F2.wireOp",EDGE,"E145.5"),sQuery(id+"F2.wireOp",EDGE,"E151"),subQ0,sQuery(id+"F2.wireOp",EDGE,"E154.filletArc")])]}),makeQuery(id+"F3.opExtrude","SWEPT_BODY",BODY,{"disambiguationData":[OSD([subQ1,sQuery(id+"F2.wireOp",EDGE,"E138"),sQuery(id+"F2.wireOp",EDGE,"E139.filletArc"),subQ0,sQuery(id+"F2.wireOp",EDGE,"E145.4")])]})]});}
            var Q3;
            Q3=makeQuery(id+"F3.opExtrude","SWEPT_BODY",BODY,{"disambiguationData":[OSD([sQuery(id+"F2.wireOp",EDGE,"E136.1"),sQuery(id+"F2.wireOp",EDGE,"E136.2"),sQuery(id+"F2.wireOp",EDGE,"E136.3"),sQuery(id+"F2.wireOp",EDGE,"E145.5"),sQuery(id+"F2.wireOp",EDGE,"E155.1"),sQuery(id+"F2.wireOp",EDGE,"E155.2")])]});
            var Q4;
            Q4=makeQuery(id+"F3.opExtrude","SWEPT_BODY",BODY,{"disambiguationData":[OSD([sQuery(id+"F2.wireOp",EDGE,"E137"),sQuery(id+"F2.wireOp",EDGE,"E145.4"),sQuery(id+"F2.wireOp",EDGE,"E145.5"),sQuery(id+"F2.wireOp",EDGE,"E151"),sQuery(id+"F2.wireOp",EDGE,"E152"),sQuery(id+"F2.wireOp",EDGE,"E154.filletArc")])]});
            var Q5;
            Q5=makeQuery(id+"F3.opExtrude","SWEPT_BODY",BODY,{"disambiguationData":[OSD([sQuery(id+"F2.wireOp",EDGE,"E136.1"),sQuery(id+"F2.wireOp",EDGE,"E145.3"),sQuery(id+"F2.wireOp",EDGE,"E155.3"),sQuery(id+"F2.wireOp",EDGE,"E156"),sQuery(id+"F2.wireOp",EDGE,"E157"),sQuery(id+"F2.wireOp",EDGE,"E158.filletArc")])]});
            booleanBodies(context, id + "F5", {"operationType" : BooleanOperationType.UNION, "tools" : qUnion([Q0, Q1, Q2, Q3, Q4, Q5])});
        }
    });
